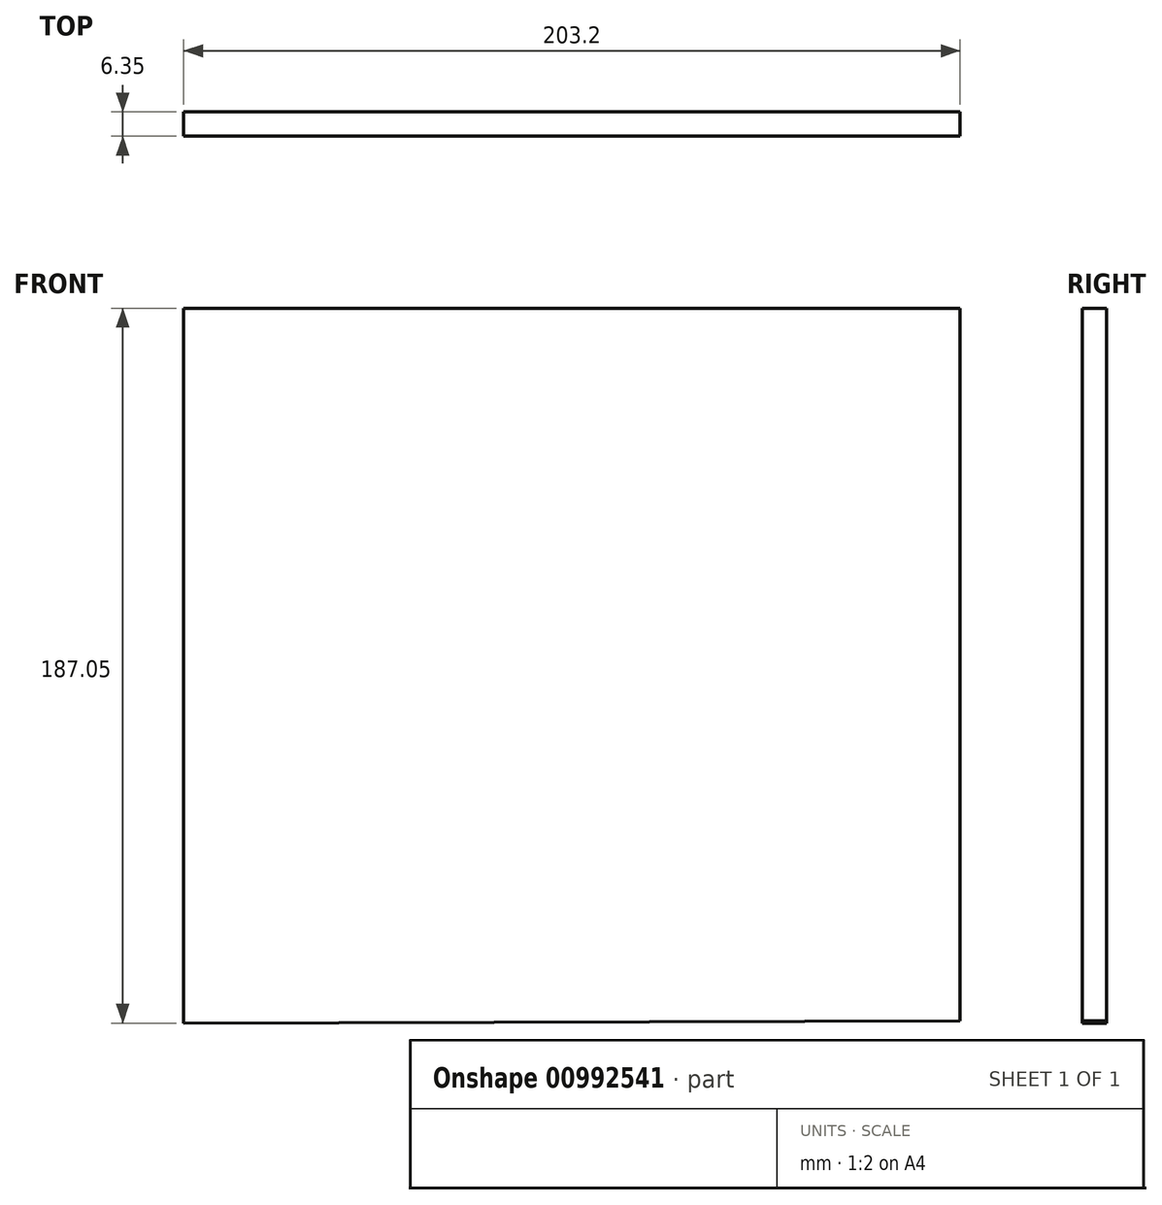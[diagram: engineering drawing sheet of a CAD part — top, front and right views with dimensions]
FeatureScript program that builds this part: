
annotation { "Feature Type Name" : "Feature", "Feature Type Description" : "" }
export const myFeature = defineFeature(function(context is Context, id is Id, definition is map)
    precondition{}
    {
        {
            var Q0;
            Q0=qCreatedBy(makeId("Front.planeOp"),FACE);
            var sketch = newSketch(context, id + "F0", { "sketchPlane" : qUnion([Q0])});
            skLineSegment(sketch, "E0", {"start": v(0, 95.5) * mm, "end": v(0, -91.02) * mm});
            skLineSegment(sketch, "E1", {"start": v(0, 95.5) * mm, "end": v(-203.2, 95.5) * mm});
            skLineSegment(sketch, "E2", {"start": v(-203.2, 95.5) * mm, "end": v(-203.2, -91.56) * mm});
            skLineSegment(sketch, "E3", {"start": v(-203.2, -91.56) * mm, "end": v(0, -91.02) * mm});
            skSolve(sketch);
        }
        {
            var Q0;
            Q0=makeQuery(id+"F0.imprint","IMPRINT",FACE,{"disambiguationData":[TD([[makeQuery(id+"F0.imprint","IMPRINT",EDGE,{"derivedFrom":sQuery(id+"F0.wireOp",EDGE,"E0")}),-1.0]])]});
            extrude(context, id + "F1", {"entities" : qUnion([Q0]), "depth" : 6.35 * mm, "offsetDistance" : 25.4 * mm});
        }
    });
